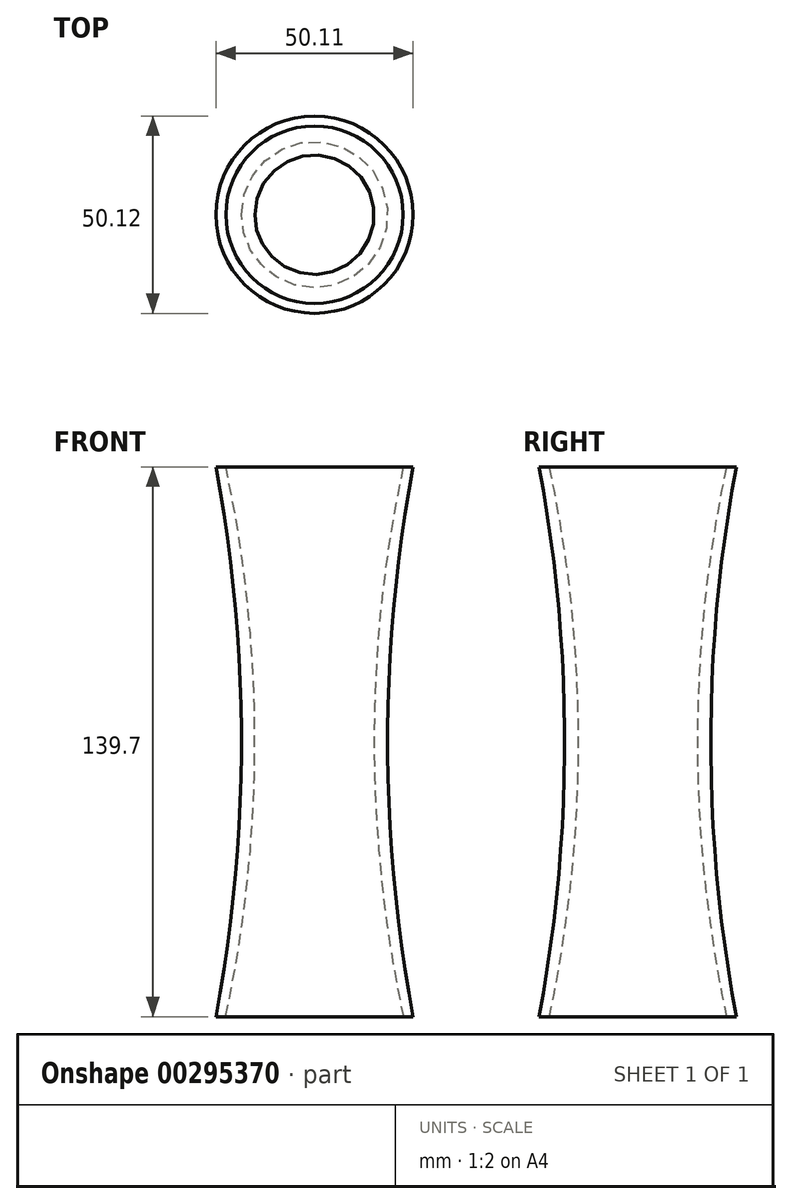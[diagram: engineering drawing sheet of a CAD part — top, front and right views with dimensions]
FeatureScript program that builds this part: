
annotation { "Feature Type Name" : "Feature", "Feature Type Description" : "" }
export const myFeature = defineFeature(function(context is Context, id is Id, definition is map)
    precondition{}
    {
        {
            var Q0;
            Q0=qCreatedBy(makeId("Front.planeOp"),FACE);
            var sketch = newSketch(context, id + "F0", { "sketchPlane" : qUnion([Q0])});
            skLineSegment(sketch, "E0.bottom", {"start": v(-16.41, -40.59) * mm, "end": v(33.7, -40.59) * mm});
            skLineSegment(sketch, "E0.top", {"start": v(-16.41, 99.11) * mm, "end": v(33.7, 99.11) * mm});
            skLineSegment(sketch, "E0.left", {"start": v(-16.41, -40.59) * mm, "end": v(-16.41, 99.11) * mm});
            skLineSegment(sketch, "E0.right", {"start": v(33.7, -40.59) * mm, "end": v(33.7, 99.11) * mm});
            skArc(sketch, "E1", {"start": v(-16.41, -40.59) * mm, "mid": v(-9.92, 29.26) * mm, "end": v(-16.41, 99.11) * mm});
            skArc(sketch, "E2", {"start": v(33.7, 99.11) * mm, "mid": v(28.05, 29.26) * mm, "end": v(33.7, -40.59) * mm});
            skLineSegment(sketch, "E3", {"start": v(8.65, -40.59) * mm, "end": v(8.65, 99.11) * mm});
            skArc(sketch, "E4", {"start": v(-13.92, -40.59) * mm, "mid": v(-6.52, 29.26) * mm, "end": v(-13.87, 99.11) * mm});
            skArc(sketch, "E5", {"start": v(31.16, 99.11) * mm, "mid": v(23.97, 29.24) * mm, "end": v(31.52, -40.59) * mm});
            skSolve(sketch);
        }
        {
            var Q0;
            {var subQ0=sQuery(id+"F0.wireOp",EDGE,"E1");Q0=makeQuery(id+"F0.imprint","IMPRINT",FACE,{"disambiguationData":[TD([[makeQuery(id+"F0.imprint","IMPRINT",EDGE,{"derivedFrom":subQ0}),-1.0]])]});}
            var Q1;
            Q1=sQuery(id+"F0.wireOp",EDGE,"E3");
            revolve(context, id + "F1", {"entities" : qUnion([Q0]), "axis" : qUnion([Q1]), "revolveType" : RevolveType.FULL});
        }
    });
